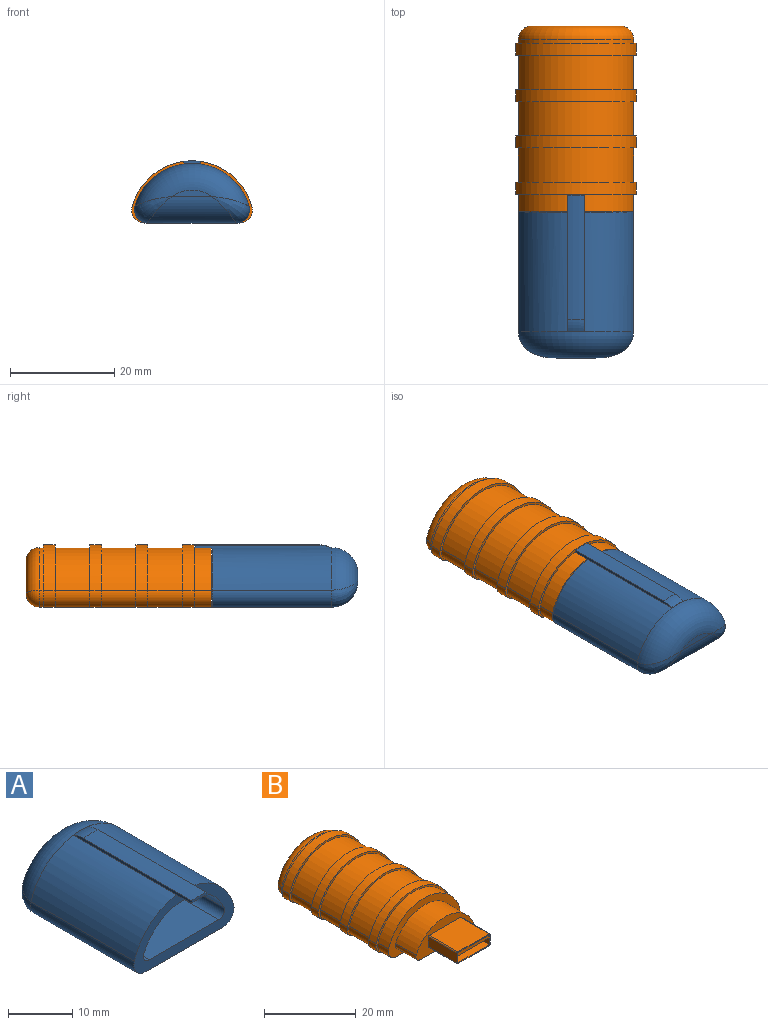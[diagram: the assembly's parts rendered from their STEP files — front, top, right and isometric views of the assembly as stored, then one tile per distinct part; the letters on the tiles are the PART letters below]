
ASSEMBLY  parts=2 mates=1
PART A: 21 faces, bbox 23.9x31.3x12.4 mm
  f0: cylinder r=11.43mm len=22.86mm, axis (0,1,0), area 595.5mm2, adj f2,f7,f8,f13,f17,f18,f20
  f1: plane 22.86x17.04mm, normal (0,0,-1), area 389.5mm2, adj f2,f7,f8,f12
  f2: plane 22.12x11.43mm, normal (0,-1,0), area 94.6mm2, adj f0,f1,f4,f5,f7,f8,f9,f10
  f3: plane 7.62x1.27mm, normal (0,1,0), area 6.6mm2, adj f12,f13
  f4: plane 15.62x15.37mm, normal (0,0,1), area 240mm2, adj f2,f6,f9,f10
  f5: cylinder r=9.59mm len=17.71mm, axis (0,-1,0), area 352.7mm2, adj f2,f6,f9,f10
  f6: plane 17.91x7.67mm, normal (0,-1,0), area 106.5mm2, adj f4,f5,f9,f10
  f7: cylinder r=2.54mm len=22.86mm, axis (0,1,0), area 108mm2, adj f0,f1,f2,f14
  f8: cylinder r=2.54mm len=22.86mm, axis (0,1,0), area 108mm2, adj f0,f1,f2,f11
  f9: cylinder r=1.27mm len=15.62mm, axis (0,-1,0), area 39mm2, adj f2,f4,f5,f6
  f10: cylinder r=1.27mm len=15.62mm, axis (0,-1,0), area 39mm2, adj f2,f4,f5,f6
  f11: bspline ~8.12x6.6mm, area 28.6mm2, adj f8,f12,f13
  f12: cylinder r=5.08mm len=17.04mm, axis (1,0,0), area 112.4mm2, adj f1,f3,f11,f14
  f13: torus R=6.35mm, axis (0,-1,0), area 172mm2, adj f0,f3,f11,f14
  f14: bspline ~8.12x6.6mm, area 28.6mm2, adj f7,f12,f13
  f15: cylinder r=11.43mm len=3.3mm, axis (0,1,0), area 10.7mm2, adj f2,f17,f18,f19
  f16: cylinder r=11.94mm len=23.9mm, axis (0,1,0), area 77.4mm2, adj f17,f18,f19,f20
  f17: plane 26.15x0.55mm, normal (-1,0,0), area 13mm2, adj f0,f15,f16,f19,f20
  f18: plane 26.15x0.55mm, normal (1,0,0), area 13mm2, adj f0,f15,f16,f19,f20
  f19: plane 3.23x0.62mm, normal (0,-1,0), area 1.6mm2, adj f15,f16,f17,f18
  f20: torus R=6.86mm, axis (0,1,0), area 7.5mm2, adj f0,f16,f17,f18
PART B: 63 faces, bbox 23.7x50.8x12.4 mm
  f0: cylinder r=11.43mm len=21.91mm, axis (0,-1,0), area 22.3mm2, adj f1,f2,f51,f61
  f1: cylinder r=2.54mm len=3.27mm, axis (0,-1,0), area 3.6mm2, adj f0,f15,f51,f59
  f2: cylinder r=2.54mm len=3.27mm, axis (0,-1,0), area 3.6mm2, adj f0,f15,f51,f62
  f3: cylinder r=11.43mm len=21.91mm, axis (0,-1,0), area 193.4mm2, adj f4,f5,f48,f52
  f4: cylinder r=2.54mm len=6.6mm, axis (0,-1,0), area 31.2mm2, adj f3,f15,f48,f52
  f5: cylinder r=2.54mm len=6.6mm, axis (0,-1,0), area 31.2mm2, adj f3,f15,f48,f52
  f6: cylinder r=11.43mm len=21.91mm, axis (0,-1,0), area 193.4mm2, adj f7,f8,f45,f49
  f7: cylinder r=2.54mm len=6.6mm, axis (0,-1,0), area 31.2mm2, adj f6,f15,f45,f49
  f8: cylinder r=2.54mm len=6.6mm, axis (0,-1,0), area 31.2mm2, adj f6,f15,f45,f49
  f9: cylinder r=11.43mm len=21.91mm, axis (0,-1,0), area 193.4mm2, adj f10,f11,f40,f46
  f10: cylinder r=2.54mm len=6.6mm, axis (0,-1,0), area 31.2mm2, adj f9,f15,f40,f46
  f11: cylinder r=2.54mm len=6.6mm, axis (0,-1,0), area 31.2mm2, adj f9,f15,f40,f46
  f12: plane 10.16x3.18mm, normal (0,-1,0), area 6.5mm2, adj f20,f21,f22,f23,f24,f25,f26,f27
  f13: plane 17.78x7.62mm, normal (0,-1,0), area 72.8mm2, adj f18,f19,f20,f21,f22,f23,f24,f25
  f14: cylinder r=11.43mm len=21.91mm, axis (0,-1,0), area 96.7mm2, adj f17,f28,f29,f41
  f15: plane 33.02x18.1mm, normal (0,0,-1), area 572.3mm2, adj f1,f2,f4,f5,f7,f8,f10,f11
  f16: plane 17.04x6.35mm, normal (0,1,0), area 79.6mm2, adj f60,f61
  f17: plane 22.12x11.43mm, normal (0,-1,0), area 96mm2, adj f14,f15,f18,f19,f28,f29,f30,f31
  f18: plane 15.24x6.35mm, normal (0,0,-1), area 96.8mm2, adj f13,f17,f30,f31
  f19: cylinder r=9.53mm len=17.58mm, axis (0,1,0), area 142.3mm2, adj f13,f17,f30,f31
  f20: plane 9.65x8.89mm, normal (0,0,-1), area 85.8mm2, adj f12,f13,f24,f27
  f21: plane 8.89x2.67mm, normal (1,0,0), area 23.7mm2, adj f12,f13,f24,f25
  f22: plane 9.65x8.89mm, normal (0,0,1), area 85.8mm2, adj f12,f13,f25,f26
  f23: plane 8.89x2.67mm, normal (-1,0,0), area 23.7mm2, adj f12,f13,f26,f27
  f24: cylinder r=0.25mm len=8.89mm, axis (0,-1,0), area 3.5mm2, adj f12,f13,f20,f21
  f25: cylinder r=0.25mm len=8.89mm, axis (0,1,0), area 3.5mm2, adj f12,f13,f21,f22
  f26: cylinder r=0.25mm len=8.89mm, axis (0,-1,0), area 3.5mm2, adj f12,f13,f22,f23
  f27: cylinder r=0.25mm len=8.89mm, axis (0,1,0), area 3.5mm2, adj f12,f13,f20,f23
  f28: cylinder r=2.54mm len=3.3mm, axis (0,-1,0), area 15.6mm2, adj f14,f15,f17,f41
  f29: cylinder r=2.54mm len=3.3mm, axis (0,-1,0), area 15.6mm2, adj f14,f15,f17,f41
  f30: cylinder r=1.27mm len=6.35mm, axis (0,1,0), area 15.9mm2, adj f13,f17,f18,f19
  f31: cylinder r=1.27mm len=6.35mm, axis (0,1,0), area 15.9mm2, adj f13,f17,f18,f19
  f32: plane 9.65x5.08mm, normal (0,0,1), area 49mm2, adj f12,f33,f35,f36
  f33: plane 5.08x2.67mm, normal (-1,0,0), area 8.8mm2, adj f12,f32,f34,f36,f37,f38
  f34: plane 9.65x4.95mm, normal (0,0,-1), area 47.8mm2, adj f33,f35,f36,f38
  f35: plane 5.08x2.67mm, normal (1,0,0), area 8.8mm2, adj f12,f32,f34,f36,f37,f38
  f36: plane 9.65x1.7mm, normal (0,-1,0), area 16.4mm2, adj f32,f33,f34,f35
  f37: plane 9.65x0.13mm, normal (0,0,-1), area 1.2mm2, adj f12,f33,f35,f38
  f38: plane 9.65x0.96mm, normal (0,-1,0), area 9.3mm2, adj f33,f34,f35,f37
  f39: cylinder r=11.94mm len=22.99mm, axis (0,-1,0), area 70.8mm2, adj f40,f41,f42,f43
  f40: plane 23.18x11.94mm, normal (0,1,0), area 18.7mm2, adj f9,f10,f11,f15,f39,f42,f43
  f41: plane 23.18x11.94mm, normal (0,-1,0), area 18.7mm2, adj f14,f15,f28,f29,f39,f42,f43
  f42: cylinder r=2.54mm len=3.23mm, axis (0,-1,0), area 10.7mm2, adj f15,f39,f40,f41
  f43: cylinder r=2.54mm len=3.23mm, axis (0,-1,0), area 10.7mm2, adj f15,f39,f40,f41
  f44: cylinder r=11.94mm len=22.99mm, axis (0,-1,0), area 70.8mm2, adj f45,f46,f57,f58
  f45: plane 23.18x11.94mm, normal (0,1,0), area 18.7mm2, adj f6,f7,f8,f15,f44,f57,f58
  f46: plane 23.18x11.94mm, normal (0,-1,0), area 18.7mm2, adj f9,f10,f11,f15,f44,f57,f58
  f47: cylinder r=11.94mm len=22.99mm, axis (0,-1,0), area 70.8mm2, adj f48,f49,f55,f56
  f48: plane 23.18x11.94mm, normal (0,1,0), area 18.7mm2, adj f3,f4,f5,f15,f47,f55,f56
  f49: plane 23.18x11.94mm, normal (0,-1,0), area 18.7mm2, adj f6,f7,f8,f15,f47,f55,f56
  f50: cylinder r=11.94mm len=22.99mm, axis (0,-1,0), area 70.8mm2, adj f51,f52,f53,f54
  f51: plane 23.18x11.94mm, normal (0,1,0), area 18.7mm2, adj f0,f1,f2,f15,f50,f53,f54
  f52: plane 23.18x11.94mm, normal (0,-1,0), area 18.7mm2, adj f3,f4,f5,f15,f50,f53,f54
  f53: cylinder r=2.54mm len=3.23mm, axis (0,-1,0), area 10.7mm2, adj f15,f50,f51,f52
  f54: cylinder r=2.54mm len=3.23mm, axis (0,-1,0), area 10.7mm2, adj f15,f50,f51,f52
  f55: cylinder r=2.54mm len=3.23mm, axis (0,-1,0), area 10.7mm2, adj f15,f47,f48,f49
  f56: cylinder r=2.54mm len=3.23mm, axis (0,-1,0), area 10.7mm2, adj f15,f47,f48,f49
  f57: cylinder r=2.54mm len=3.23mm, axis (0,-1,0), area 10.7mm2, adj f15,f44,f45,f46
  f58: cylinder r=2.54mm len=3.23mm, axis (0,-1,0), area 10.7mm2, adj f15,f44,f45,f46
  f59: sphere r=2.54mm, area 12mm2, adj f1,f60,f61
  f60: cylinder r=2.54mm len=17.04mm, axis (-1,0,0), area 68mm2, adj f15,f16,f59,f62
  f61: torus R=8.89mm, axis (0,-1,0), area 107.4mm2, adj f0,f16,f59,f62
  f62: sphere r=2.54mm, area 12mm2, adj f2,f60,f61
PLACE A rot(axis=(0,0,1),180deg) t=(9.03,-35.48,-6.92)mm
PLACE B t=(9.03,-7.38,-6.92)mm
MATE slider A.f5 <-> B.f19  axis (0,1,0) through (9.03,-7.54,-6.92)mm
